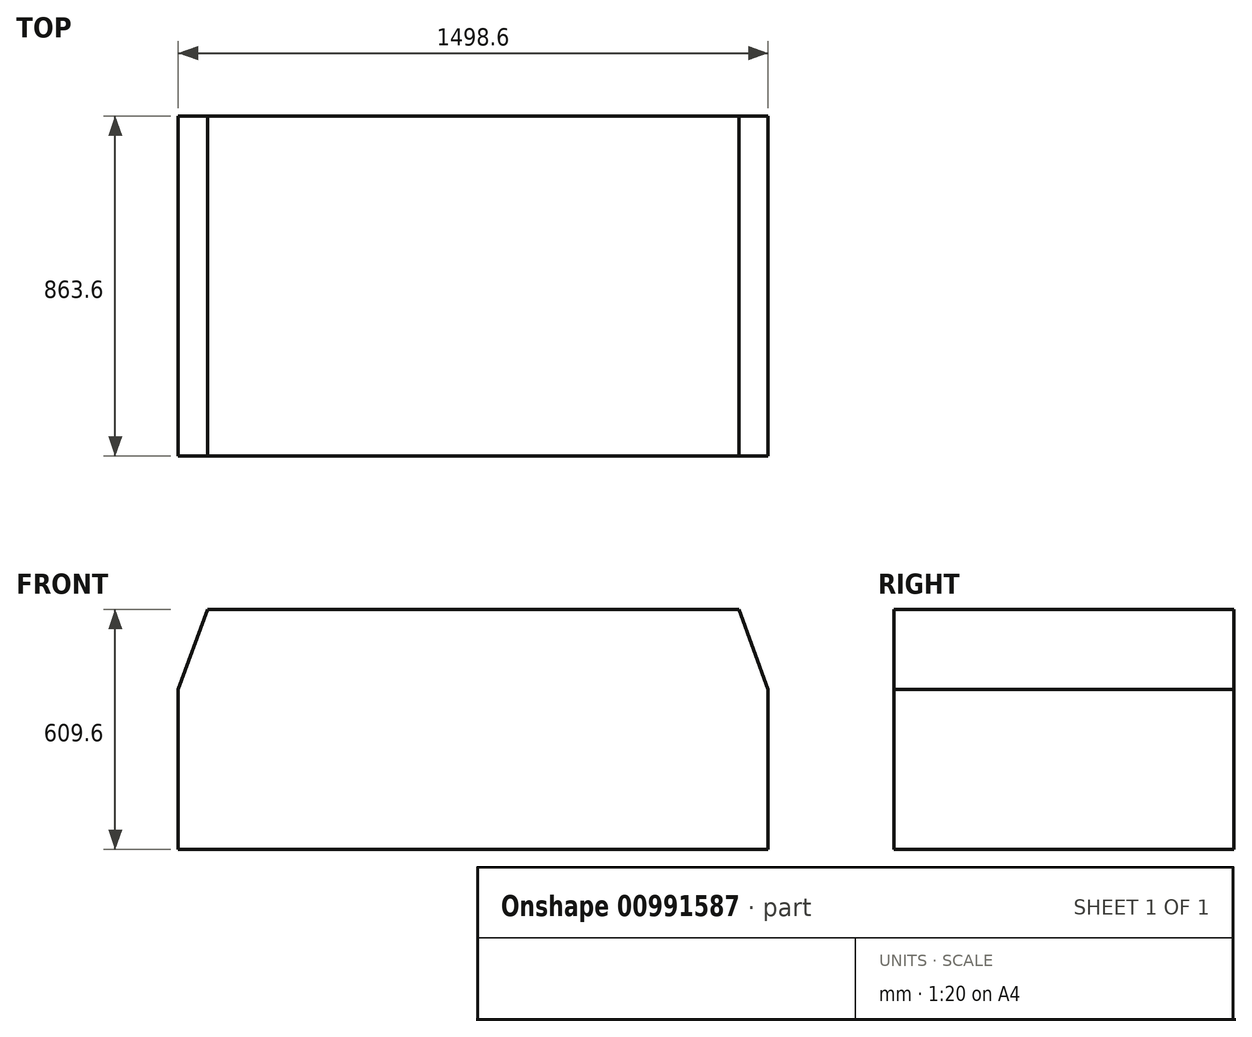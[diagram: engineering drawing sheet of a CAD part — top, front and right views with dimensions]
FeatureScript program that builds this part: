
annotation { "Feature Type Name" : "Feature", "Feature Type Description" : "" }
export const myFeature = defineFeature(function(context is Context, id is Id, definition is map)
    precondition{}
    {
        {
            var Q0;
            Q0=qCreatedBy(makeId("Top.planeOp"),FACE);
            var sketch = newSketch(context, id + "F0", { "sketchPlane" : qUnion([Q0])});
            skLineSegment(sketch, "E0.bottom", {"start": v(749.3, -431.8) * mm, "end": v(-749.3, -431.8) * mm});
            skLineSegment(sketch, "E0.top", {"start": v(749.3, 431.8) * mm, "end": v(-749.3, 431.8) * mm});
            skLineSegment(sketch, "E0.left", {"start": v(749.3, -431.8) * mm, "end": v(749.3, 431.8) * mm});
            skLineSegment(sketch, "E0.right", {"start": v(-749.3, -431.8) * mm, "end": v(-749.3, 431.8) * mm});
            skPoint(sketch, "E0.middle", {"position": v(0, 0) * mm});
            skSolve(sketch);
        }
        {
            var Q0;
            Q0=makeQuery(id+"F0.imprint","IMPRINT",FACE,{"disambiguationData":[TD([[makeQuery(id+"F0.imprint","IMPRINT",EDGE,{"derivedFrom":sQuery(id+"F0.wireOp",EDGE,"E0.bottom")}),-1.0]])]});
            extrude(context, id + "F1", {"entities" : qUnion([Q0]), "depth" : 609.6 * mm, "offsetDistance" : 25.4 * mm});
        }
        {
            var Q0;
            Q0=makeQuery(id+"F1.opExtrude","CAP_EDGE",EDGE,{"disambiguationData":[OSD([sQuery(id+"F0.wireOp",EDGE,"E0.right")])],"isStart":false});
            var Q1;
            Q1=makeQuery(id+"F1.opExtrude","CAP_EDGE",EDGE,{"disambiguationData":[OSD([sQuery(id+"F0.wireOp",EDGE,"E0.left")])],"isStart":false});
            chamfer(context, id + "F2", {"entities" : qUnion([Q0, Q1]), "chamferType" : ChamferType.OFFSET_ANGLE, "width" : 203.2 * mm, "oppositeDirection" : false, "angle" : 20 * degree, "tangentPropagation" : true});
        }
    });
